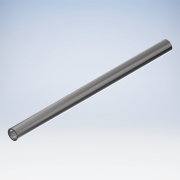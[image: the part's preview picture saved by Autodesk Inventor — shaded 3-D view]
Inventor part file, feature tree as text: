
AUTODESK INVENTOR PART (.ipt)
format: ipt  version: 2018.2 (Build 222227000, 227)  size: 98,816 bytes
history: native  units: mm
features: extrude x1, chamfer x1, sketch x1
ambient origin geometry x8: Origin, YZ Plane, XZ Plane, XY Plane, X Axis, Y Axis, Z Axis, Center Point
bodies: Solid1 (feature_tree)
feature tree (3):
  extrude  "Extrusion1"  Depth=150.0mm
  chamfer  "Chamfer1"  Distance=150.0mm
  sketch  "Sketch1"  dims[d0=6.55mm d1=9.6mm d2=150.0mm d3=0.0mm d4=0.75mm d5=2.0mm d6=45.0deg]
